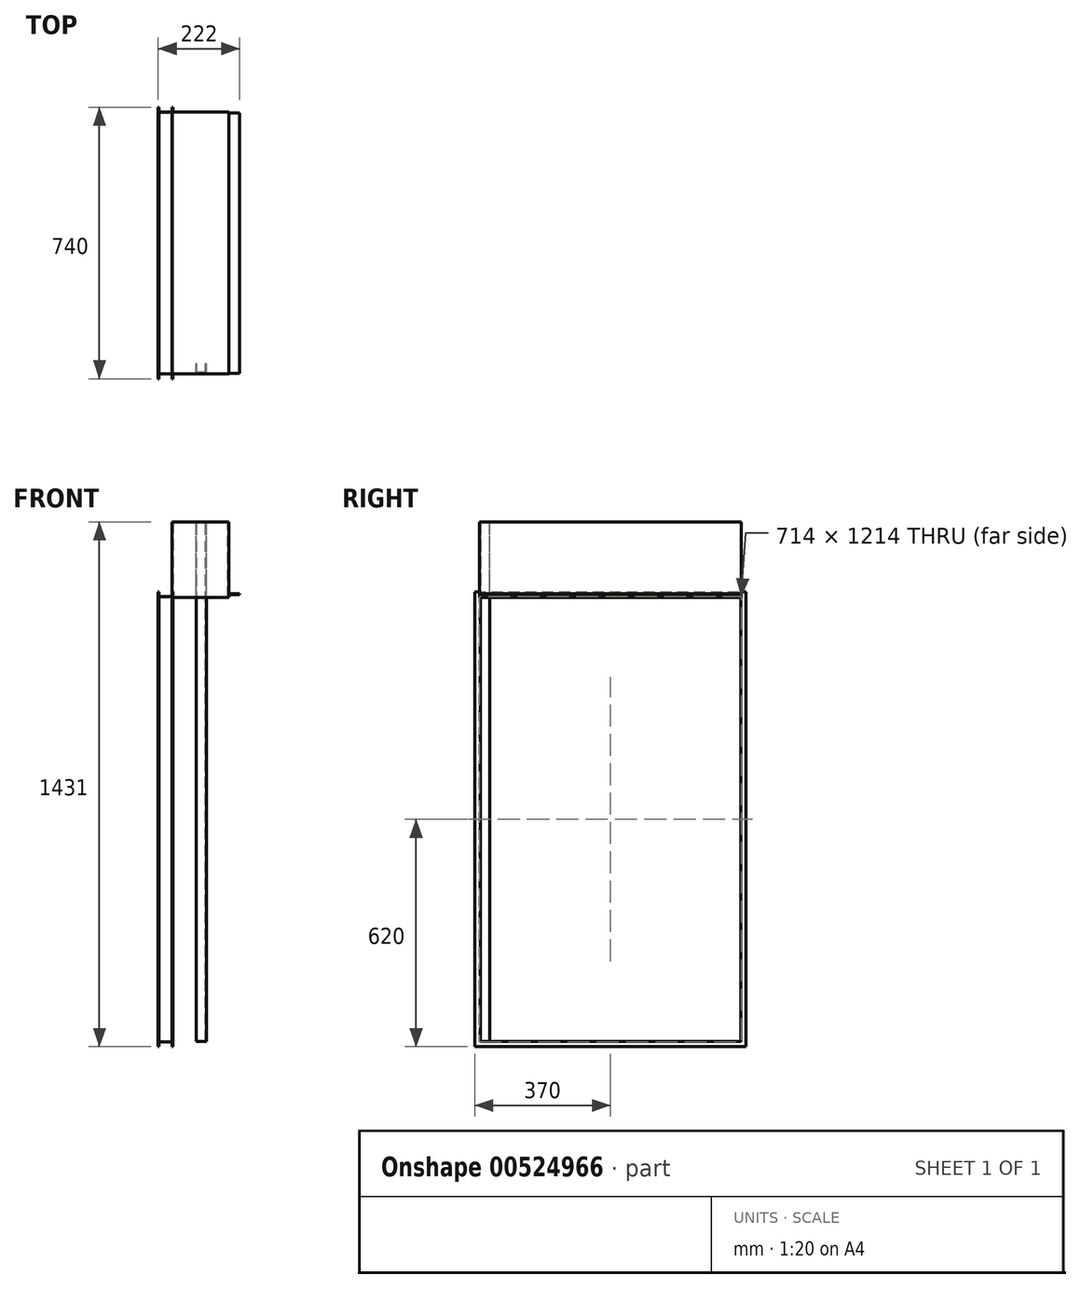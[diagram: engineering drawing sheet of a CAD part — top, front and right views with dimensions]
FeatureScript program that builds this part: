
annotation { "Feature Type Name" : "Feature", "Feature Type Description" : "" }
export const myFeature = defineFeature(function(context is Context, id is Id, definition is map)
    precondition{}
    {
        {
            var Q0;
            Q0=qCreatedBy(makeId("Front.planeOp"),FACE);
            var sketch = newSketch(context, id + "F0", { "sketchPlane" : qUnion([Q0])});
            skLineSegment(sketch, "E0", {"start": v(0, 0) * mm, "end": v(0, 206) * mm});
            skLineSegment(sketch, "E1", {"start": v(0, 206) * mm, "end": v(-154, 206) * mm});
            skLineSegment(sketch, "E2", {"start": v(-154, 206) * mm, "end": v(-154, 0) * mm});
            skLineSegment(sketch, "E3", {"start": v(0, 10) * mm, "end": v(30, 10) * mm});
            skLineSegment(sketch, "E4.0", {"start": v(-152, 204) * mm, "end": v(-152, 0) * mm});
            skLineSegment(sketch, "E4.1", {"start": v(-2, 204) * mm, "end": v(-152, 204) * mm});
            skLineSegment(sketch, "E4.2", {"start": v(-2, 0) * mm, "end": v(-2, 204) * mm});
            skLineSegment(sketch, "E5.0", {"start": v(0, 8) * mm, "end": v(30, 8) * mm});
            skLineSegment(sketch, "E6", {"start": v(-154, 0) * mm, "end": v(-152, 0) * mm});
            skLineSegment(sketch, "E7", {"start": v(30, 8) * mm, "end": v(30, 10) * mm});
            skLineSegment(sketch, "E8", {"start": v(-2, 0) * mm, "end": v(0, 0) * mm});
            skPoint(sketch, "E9.start.orphan", {"position": v(-150, -15) * mm});
            skPoint(sketch, "E10.start.orphan", {"position": v(-190, -15) * mm});
            skSolve(sketch);
        }
        {
            var Q0;
            {var subQ3=sQuery(id+"F0.wireOp",EDGE,"E1");Q0=makeQuery(id+"F0.imprint","IMPRINT",FACE,{"disambiguationData":[TD([[makeQuery(id+"F0.imprint","IMPRINT",EDGE,{"derivedFrom":subQ3}),1.0]])]});}
            var Q1;
            {var subQ0=sQuery(id+"F0.wireOp",EDGE,"E3");Q1=makeQuery(id+"F0.imprint","IMPRINT",FACE,{"disambiguationData":[TD([[makeQuery(id+"F0.imprint","IMPRINT",EDGE,{"derivedFrom":subQ0}),-1.0]])]});}
            extrude(context, id + "F1", {"entities" : qUnion([Q0, Q1]), "oppositeDirection" : true, "depth" : 710 * mm, "offsetDistance" : 25 * mm});
        }
        {
            var Q0;
            Q0=makeQuery(id+"F1.opExtrude","SWEPT_FACE",FACE,{"disambiguationData":[OSD([sQuery(id+"F0.wireOp",EDGE,"E4.0")])]});
            cPlane(context, id + "F2", {"entities" : qUnion([Q0]), "cplaneType" : CPlaneType.OFFSET, "offset" : 0 * mm, "width" : 150 * mm, "height" : 150 * mm});
        }
        {
            var Q0;
            Q0=qCreatedBy(id+"F2.planeOp",FACE);
            var sketch = newSketch(context, id + "F3", { "sketchPlane" : qUnion([Q0])});
            skLineSegment(sketch, "E11.bottom", {"start": v(0, 0) * mm, "end": v(710, 0) * mm});
            skLineSegment(sketch, "E11.top", {"start": v(0, -1210) * mm, "end": v(710, -1210) * mm});
            skLineSegment(sketch, "E11.left", {"start": v(0, 0) * mm, "end": v(0, -1210) * mm});
            skLineSegment(sketch, "E11.right", {"start": v(710, 0) * mm, "end": v(710, -1210) * mm});
            skSolve(sketch);
        }
        {
            var Q0;
            {var subQ0=sQuery(id+"F0.wireOp",EDGE,"E1");Q0=makeQuery(id+"F0.imprint","IMPRINT",FACE,{"disambiguationData":[TD([[makeQuery(id+"F0.imprint","IMPRINT",EDGE,{"derivedFrom":subQ0}),1.0]])]});}
            cPlane(context, id + "F4", {"entities" : qUnion([Q0]), "cplaneType" : CPlaneType.OFFSET, "offset" : 0 * mm, "width" : 150 * mm, "height" : 150 * mm});
        }
        {
            var Q0;
            Q0=qCreatedBy(id+"F4.planeOp",FACE);
            var sketch = newSketch(context, id + "F5", { "sketchPlane" : qUnion([Q0])});
            skLineSegment(sketch, "E12", {"start": v(-152, 0) * mm, "end": v(-152, 15) * mm});
            skLineSegment(sketch, "E13", {"start": v(-192, 15) * mm, "end": v(-192, 0) * mm});
            skLineSegment(sketch, "E14", {"start": v(-192, 0) * mm, "end": v(-152, 0) * mm});
            skLineSegment(sketch, "E15.0", {"start": v(-154, 2) * mm, "end": v(-154, 15) * mm});
            skLineSegment(sketch, "E15.1", {"start": v(-190, 2) * mm, "end": v(-154, 2) * mm});
            skLineSegment(sketch, "E15.2", {"start": v(-190, 15) * mm, "end": v(-190, 2) * mm});
            skLineSegment(sketch, "E16", {"start": v(-192, 15) * mm, "end": v(-190, 15) * mm});
            skLineSegment(sketch, "E17", {"start": v(-154, 15) * mm, "end": v(-152, 15) * mm});
            skSolve(sketch);
        }
        {
            var Q0;
            Q0=makeQuery(id+"F5.imprint","IMPRINT",FACE,{"disambiguationData":[TD([[makeQuery(id+"F5.imprint","IMPRINT",EDGE,{"derivedFrom":sQuery(id+"F5.wireOp",EDGE,"E12")}),1.0]])]});
            var Q1;
            Q1=qConstructionFilter(qBodyType(qCreatedBy(id+"F3",EDGE),BodyType.WIRE),ConstructionObject.NO);
            sweep(context, id + "F6", {"operationType" : NewBodyOperationType.ADD, "profiles" : qUnion([Q0]), "path" : qUnion([Q1])});
        }
        {
            var Q0;
            Q0=makeQuery(id+"F1.opExtrude","SWEPT_FACE",FACE,{"disambiguationData":[OSD([sQuery(id+"F0.wireOp",EDGE,"E4.1")])]});
            var sketch = newSketch(context, id + "F7", { "sketchPlane" : qUnion([Q0])});
            skLineSegment(sketch, "E18.bottom", {"start": v(-77, 0) * mm, "end": v(-89, 0) * mm});
            skLineSegment(sketch, "E18.top", {"start": v(-87, -26) * mm, "end": v(-89, -26) * mm});
            skLineSegment(sketch, "E18.right", {"start": v(-89, 0) * mm, "end": v(-89, -26) * mm});
            skLineSegment(sketch, "E19.MirrorCS", {"start": v(-63, -26) * mm, "end": v(-61, -26) * mm});
            skLineSegment(sketch, "E20.MirrorCS", {"start": v(-61, 0) * mm, "end": v(-61, -26) * mm});
            skLineSegment(sketch, "E21.MirrorCS", {"start": v(-75, 0) * mm, "end": v(-61, 0) * mm});
            skLineSegment(sketch, "E22.0", {"start": v(-87, -2) * mm, "end": v(-87, -26) * mm});
            skLineSegment(sketch, "E22.1", {"start": v(-75, -2) * mm, "end": v(-87, -2) * mm});
            skLineSegment(sketch, "E22.2", {"start": v(-75, -2) * mm, "end": v(-63, -2) * mm});
            skLineSegment(sketch, "E22.3", {"start": v(-63, -2) * mm, "end": v(-63, -26) * mm});
            skPoint(sketch, "E23.orphan", {"position": v(-75, -26) * mm});
            skSolve(sketch);
        }
        {
            var Q0;
            Q0=makeQuery(id+"F7.imprint","IMPRINT",FACE,{"disambiguationData":[TD([[makeQuery(id+"F7.imprint","IMPRINT",EDGE,{"derivedFrom":sQuery(id+"F7.wireOp",EDGE,"E18.bottom")}),1.0]])]});
            var Q1;
            Q1=makeQuery(id+"F6.opSweep","SWEPT_FACE",FACE,{"disambiguationData":[OSD([sQuery(id+"F3.wireOp",EDGE,"E11.top"),sQuery(id+"F5.wireOp",EDGE,"LKxghPaX-kVdG-r2eD-1wmU-N69SjMgiJEC4")])]});
            extrude(context, id + "F8", {"entities" : qUnion([Q0]), "operationType" : NewBodyOperationType.ADD, "endBound" : BoundingType.UP_TO_SURFACE, "depth" : 1200 * mm, "endBoundEntityFace" : qUnion([Q1]), "offsetDistance" : 25 * mm});
        }
        {
            var Q0;
            {var subQ0=sQuery(id+"F0.wireOp",EDGE,"E4.1");Q0=makeQuery(id+"F8.boolean.opBoolean","MERGE",FACE,{"derivedFrom":[makeQuery(id+"F1.opExtrude","CAP_FACE",FACE,{"disambiguationData":[OSD([sQuery(id+"F0.wireOp",EDGE,"E0"),sQuery(id+"F0.wireOp",EDGE,"E1"),sQuery(id+"F0.wireOp",EDGE,"E2"),sQuery(id+"F0.wireOp",EDGE,"E3"),sQuery(id+"F0.wireOp",EDGE,"E4.0"),subQ0,sQuery(id+"F0.wireOp",EDGE,"E4.2"),sQuery(id+"F0.wireOp",EDGE,"E5.0"),sQuery(id+"F0.wireOp",EDGE,"E6"),sQuery(id+"F0.wireOp",EDGE,"E7"),sQuery(id+"F0.wireOp",EDGE,"E8")])],"isStart":true}),makeQuery(id+"F8.opExtrude","SWEPT_FACE",FACE,{"disambiguationData":[OSD([subQ0,sQuery(id+"F7.wireOp",EDGE,"E18.bottom"),sQuery(id+"F7.wireOp",EDGE,"E21.MirrorCS")])]})]});}
            var sketch = newSketch(context, id + "F9", { "sketchPlane" : qUnion([Q0])});
            skLineSegment(sketch, "E24.bottom", {"start": v(-154, 206) * mm, "end": v(0, 206) * mm});
            skLineSegment(sketch, "E24.top", {"start": v(-154, 0) * mm, "end": v(0, 0) * mm});
            skLineSegment(sketch, "E24.left", {"start": v(-154, 206) * mm, "end": v(-154, 0) * mm});
            skLineSegment(sketch, "E24.right", {"start": v(0, 206) * mm, "end": v(0, 0) * mm});
            skSolve(sketch);
        }
        {
            var Q0;
            Q0=qSketchRegion(id+"F9",true);
            extrude(context, id + "F10", {"entities" : qUnion([Q0]), "operationType" : NewBodyOperationType.ADD, "depth" : 2 * mm, "offsetDistance" : 25 * mm});
        }
        {
            var Q0;
            Q0=makeQuery(id+"F1.opExtrude","CAP_FACE",FACE,{"disambiguationData":[OSD([sQuery(id+"F0.wireOp",EDGE,"E0"),sQuery(id+"F0.wireOp",EDGE,"E1"),sQuery(id+"F0.wireOp",EDGE,"E2"),sQuery(id+"F0.wireOp",EDGE,"E3"),sQuery(id+"F0.wireOp",EDGE,"E4.0"),sQuery(id+"F0.wireOp",EDGE,"E4.1"),sQuery(id+"F0.wireOp",EDGE,"E4.2"),sQuery(id+"F0.wireOp",EDGE,"E5.0"),sQuery(id+"F0.wireOp",EDGE,"E6"),sQuery(id+"F0.wireOp",EDGE,"E7"),sQuery(id+"F0.wireOp",EDGE,"E8")])],"isStart":false});
            var sketch = newSketch(context, id + "F11", { "sketchPlane" : qUnion([Q0])});
            skLineSegment(sketch, "E25.bottom", {"start": v(154, 206) * mm, "end": v(0, 206) * mm});
            skLineSegment(sketch, "E25.top", {"start": v(154, 0) * mm, "end": v(0, 0) * mm});
            skLineSegment(sketch, "E25.left", {"start": v(154, 206) * mm, "end": v(154, 0) * mm});
            skLineSegment(sketch, "E25.right", {"start": v(0, 206) * mm, "end": v(0, 0) * mm});
            skSolve(sketch);
        }
        {
            var Q0;
            Q0=qSketchRegion(id+"F11",true);
            extrude(context, id + "F12", {"entities" : qUnion([Q0]), "operationType" : NewBodyOperationType.ADD, "depth" : 2 * mm, "offsetDistance" : 25 * mm});
        }
    });
